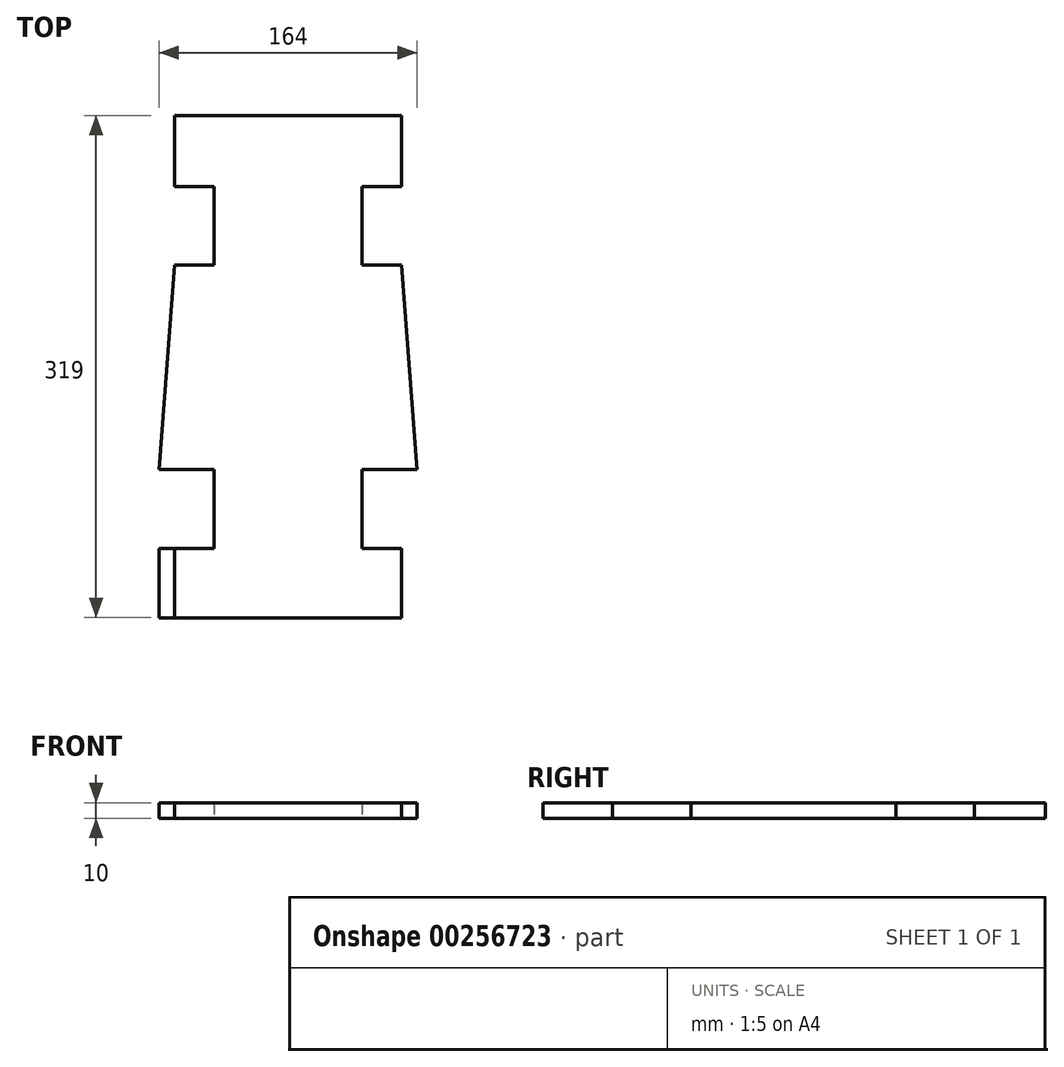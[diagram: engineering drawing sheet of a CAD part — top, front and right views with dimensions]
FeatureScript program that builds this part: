
annotation { "Feature Type Name" : "Feature", "Feature Type Description" : "" }
export const myFeature = defineFeature(function(context is Context, id is Id, definition is map)
    precondition{}
    {
        {
            var Q0;
            Q0=qCreatedBy(makeId("Top.planeOp"),FACE);
            var sketch = newSketch(context, id + "F0", { "sketchPlane" : qUnion([Q0])});
            skLineSegment(sketch, "E0.bottom", {"start": v(-72, 156.06) * mm, "end": v(0, 156.06) * mm});
            skLineSegment(sketch, "E0.top", {"start": v(-72, -162.94) * mm, "end": v(0, -162.94) * mm});
            skLineSegment(sketch, "E0.left", {"start": v(-72, 156.06) * mm, "end": v(-72, 111.06) * mm});
            skLineSegment(sketch, "E1", {"start": v(0, 156.06) * mm, "end": v(0, -162.94) * mm});
            skLineSegment(sketch, "E2.bottom", {"start": v(-72, 111.06) * mm, "end": v(-47, 111.06) * mm});
            skLineSegment(sketch, "E2.top", {"start": v(-72, 61.06) * mm, "end": v(-47, 61.06) * mm});
            skLineSegment(sketch, "E2.right", {"start": v(-47, 111.06) * mm, "end": v(-47, 61.06) * mm});
            skLineSegment(sketch, "E3.trimOffspring", {"start": v(-72, -118.94) * mm, "end": v(-72, -162.94) * mm});
            skLineSegment(sketch, "E4.bottom", {"start": v(-82, -68.94) * mm, "end": v(-72, -68.94) * mm});
            skLineSegment(sketch, "E5.MirrorCS", {"start": v(-82, -68.94) * mm, "end": v(-72, 61.06) * mm});
            skPoint(sketch, "E6.MirrorCS.start.orphan", {"position": v(-72, -68.94) * mm});
            skLineSegment(sketch, "E7.bottom", {"start": v(-72, -68.94) * mm, "end": v(-47, -68.94) * mm});
            skLineSegment(sketch, "E7.top", {"start": v(-72, -118.94) * mm, "end": v(-47, -118.94) * mm});
            skLineSegment(sketch, "E7.right", {"start": v(-47, -68.94) * mm, "end": v(-47, -118.94) * mm});
            skLineSegment(sketch, "E8.MirrorCS", {"start": v(82, -68.94) * mm, "end": v(72, 61.06) * mm});
            skLineSegment(sketch, "E9.MirrorCS", {"start": v(47, 111.06) * mm, "end": v(47, 61.06) * mm});
            skLineSegment(sketch, "E10.MirrorCS", {"start": v(72, 111.06) * mm, "end": v(47, 111.06) * mm});
            skLineSegment(sketch, "E11.MirrorCS", {"start": v(72, 156.06) * mm, "end": v(72, 111.06) * mm});
            skLineSegment(sketch, "E12.MirrorCS", {"start": v(72, 156.06) * mm, "end": v(0, 156.06) * mm});
            skLineSegment(sketch, "E13.MirrorCS", {"start": v(72, 61.06) * mm, "end": v(47, 61.06) * mm});
            skLineSegment(sketch, "E14.MirrorCS", {"start": v(72, -68.94) * mm, "end": v(47, -68.94) * mm});
            skLineSegment(sketch, "E15.MirrorCS", {"start": v(82, -68.94) * mm, "end": v(72, -68.94) * mm});
            skLineSegment(sketch, "E16.MirrorCS", {"start": v(47, -68.94) * mm, "end": v(47, -118.94) * mm});
            skLineSegment(sketch, "E17.MirrorCS", {"start": v(72, -118.94) * mm, "end": v(47, -118.94) * mm});
            skLineSegment(sketch, "E18.MirrorCS", {"start": v(72, -118.94) * mm, "end": v(72, -162.94) * mm});
            skLineSegment(sketch, "E19.MirrorCS", {"start": v(72, -162.94) * mm, "end": v(0, -162.94) * mm});
            skSolve(sketch);
        }
        {
            var Q0;
            Q0=makeQuery(id+"F0.imprint","IMPRINT",FACE,{"disambiguationData":[TD([[makeQuery(id+"F0.imprint","IMPRINT",EDGE,{"derivedFrom":sQuery(id+"F0.wireOp",EDGE,"E0.bottom")}),-1.0]])]});
            var sketch = newSketch(context, id + "F1", { "sketchPlane" : qUnion([Q0])});
            skLineSegment(sketch, "E20.bottom", {"start": v(-82, -118.94) * mm, "end": v(-72, -118.94) * mm});
            skLineSegment(sketch, "E20.top", {"start": v(-82, -162.94) * mm, "end": v(-72, -162.94) * mm});
            skLineSegment(sketch, "E20.left", {"start": v(-82, -118.94) * mm, "end": v(-82, -162.94) * mm});
            skLineSegment(sketch, "E21.MirrorCS", {"start": v(82, -118.94) * mm, "end": v(82, -162.94) * mm});
            skLineSegment(sketch, "E22.MirrorCS", {"start": v(82, -118.94) * mm, "end": v(72, -118.94) * mm});
            skLineSegment(sketch, "E23.MirrorCS", {"start": v(82, -162.94) * mm, "end": v(72, -162.94) * mm});
            skSolve(sketch);
        }
        {
            var Q0;
            Q0=makeQuery(id+"F0.imprint","IMPRINT",FACE,{"disambiguationData":[TD([[makeQuery(id+"F0.imprint","IMPRINT",EDGE,{"derivedFrom":sQuery(id+"F0.wireOp",EDGE,"E0.bottom")}),-1.0]])]});
            var Q1;
            Q1=makeQuery(id+"F0.imprint","IMPRINT",FACE,{"disambiguationData":[TD([[makeQuery(id+"F0.imprint","IMPRINT",EDGE,{"derivedFrom":sQuery(id+"F0.wireOp",EDGE,"E1")}),1.0]])]});
            var Q2;
            Q2=makeQuery(id+"F1.imprint","IMPRINT",FACE,{"disambiguationData":[TD([[makeQuery(id+"F1.imprint","IMPRINT",EDGE,{"derivedFrom":sQuery(id+"F1.wireOp",EDGE,"E20.bottom")}),-1.0]])]});
            extrude(context, id + "F2", {"entities" : qUnion([Q0, Q1, Q2]), "depth" : 10 * mm});
        }
    });
